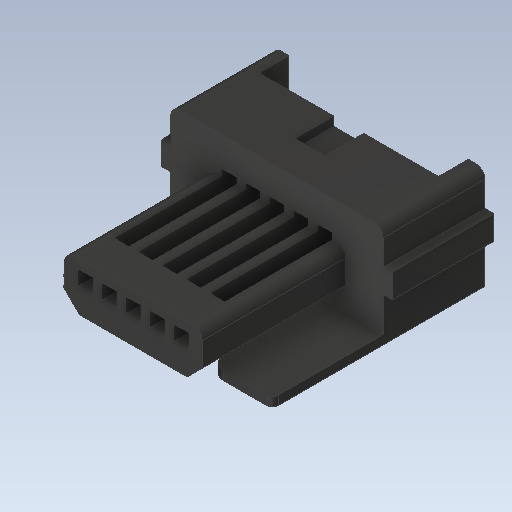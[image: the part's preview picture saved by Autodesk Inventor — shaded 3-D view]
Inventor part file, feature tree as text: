
AUTODESK INVENTOR PART (.ipt)
format: ipt  version: 2020.1 (Build 241239000, 239)  size: 204,288 bytes
history: native  units: mm
features: fillet x1
ambient origin geometry x8: Origin, YZ Plane, XZ Plane, XY Plane, X Axis, Y Axis, Z Axis, Center Point
bodies: Solid1 (feature_tree)
feature tree (1):
  fillet  "Fillet3"  [1 undecoded]
note: 1 required parameter value undecoded (feature->parameter linkage not recoverable at this tier; creation-order binding heuristic only, values carry confidence <= 0.55)
